# Revit family: Legrand_Hotel_UX_TOUCH_Door_Unit
name_source: partatom
category: Equipement électrique
units: mm (PartAtom-declared; Revit-internal decimal feet)

## family parameters
Configuration du panneau = Deux colonnes, circuits au sein
Cote de connecteur circulaire = Utiliser le diamètre
Couper avec des vides une fois chargée = Non
Hôte = Face
Partagée = Non
Point de calcul de pièce = Non
Type d'élément = Tableau de raccordement

## types (2) — shared parameters
Built-in depth = 30 mm  [stored 0.0984252 ft]
Colour = Black
Degree of impact strength (IK) = IK02
Degree of protection (IP) = IP20
Elévation par défaut = 1300 mm  [stored 4.26509 ft]
Fabricant = Legrand
General Conditions of Use = https://export.legrand.com
Material = LEGRAND - Black plastic
Mounting method = Flush mounted (plaster)
Number of buttons = 2
Operating / setting temperature MIN-MAX (°C) = 0-40
Other bus systems = Other
Overall depth = 42 mm  [stored 0.137795 ft]
Overall height = 93 mm  [stored 0.305118 ft]
Overall width = 129 mm  [stored 0.423228 ft]
Programmable = Oui
Programming way = Computer
Storage temperature MIN-MAX (°C) = -20-70
Supply frequency MIN-MAX ( Hz) = 0-0
Type of surface = Brilliant
URL = http://www.legrandoc.com
Web configurator = https://uxforupscalehotel.legrand.com
With LED indication = Oui
With room temperature controller = Non

## per-type parameters (varying)
| type | Command | Description | Modèle | Standby consuption (mA) |
| Corridor Reader | Lecteur externe SCS | External reader SCS | 048776 | 12 |
| Corridor Indicator | Indicateur externe SCS | external indicator SCS | 048775 | 8 |

note: [stored X ft] marks values corroborated as IEEE doubles in the binary element streams (Revit-internal decimal feet)
